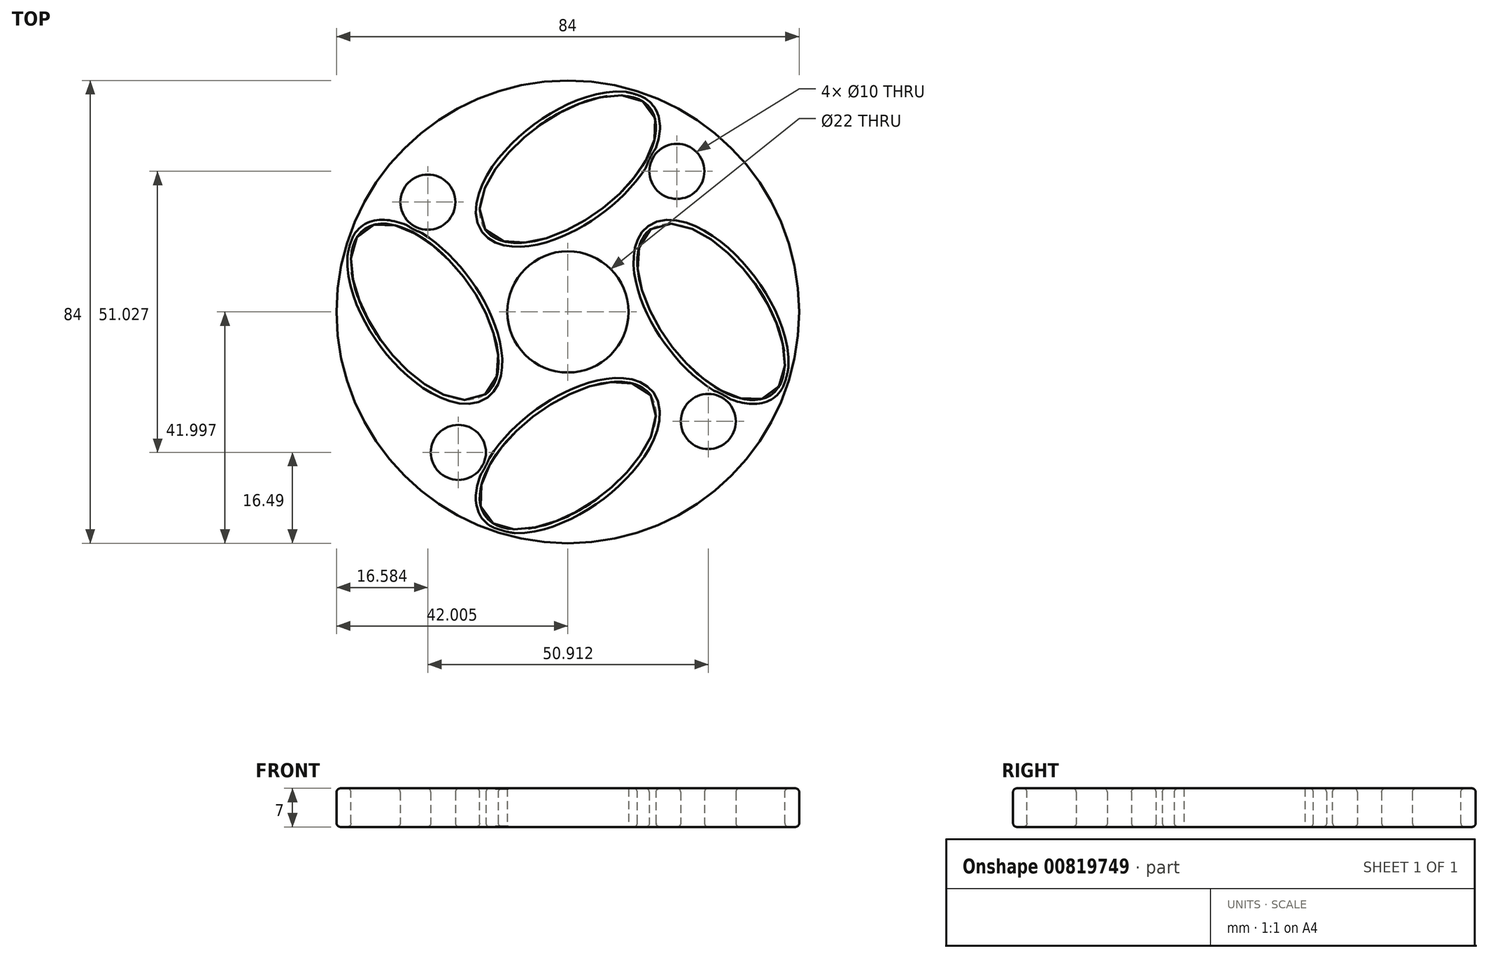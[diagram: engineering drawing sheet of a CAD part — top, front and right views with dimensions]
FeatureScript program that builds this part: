
annotation { "Feature Type Name" : "Feature", "Feature Type Description" : "" }
export const myFeature = defineFeature(function(context is Context, id is Id, definition is map)
    precondition{}
    {
        {
            var Q0;
            Q0=qCreatedBy(makeId("Top.planeOp"),FACE);
            var sketch = newSketch(context, id + "F0", { "sketchPlane" : qUnion([Q0])});
            skCircle(sketch, "E0", {"center": v(-89.33, 23.05) * mm, "radius": 11 * mm});
            skPoint(sketch, "E1", {"position": v(-100.33, 23.05) * mm});
            skPoint(sketch, "E2", {"position": v(-78.33, 23.05) * mm});
            skEllipse(sketch, "E3", {"center": v(-63.33, 23.05) * mm, "majorRadius": 18.6 * mm, "minorRadius": 9.47 * mm, "majorAxis": v(-0.6, 0.8)});
            skEllipse(sketch, "E4", {"center": v(-115.33, 23.05) * mm, "majorRadius": 18.6 * mm, "minorRadius": 9.47 * mm, "majorAxis": v(0.6, -0.8)});
            skPoint(sketch, "E5", {"position": v(-89.33, 33.96) * mm});
            skPoint(sketch, "E6", {"position": v(-89.33, 11.96) * mm});
            skEllipse(sketch, "E7", {"center": v(-89.33, -3.04) * mm, "majorRadius": 18.6 * mm, "minorRadius": 9.47 * mm, "majorAxis": v(0.8, 0.6)});
            skEllipse(sketch, "E8", {"center": v(-89.33, 48.96) * mm, "majorRadius": 18.6 * mm, "minorRadius": 9.47 * mm, "majorAxis": v(-0.8, -0.6)});
            skCircle(sketch, "E9", {"center": v(-89.33, 23.05) * mm, "radius": 42 * mm});
            skPoint(sketch, "E10", {"position": v(-103.17, 47.9) * mm});
            skPoint(sketch, "E11", {"position": v(-64.63, 37.03) * mm});
            skPoint(sketch, "E12", {"position": v(-75.34, -1.73) * mm});
            skPoint(sketch, "E13", {"position": v(-114.1, 9.12) * mm});
            skLineSegment(sketch, "E14", {"start": v(-75.34, -1.73) * mm, "end": v(-52.33, 8.05) * mm});
            skLineSegment(sketch, "E15", {"start": v(-64.63, 37.03) * mm, "end": v(-74.43, 60.1) * mm});
            skLineSegment(sketch, "E16", {"start": v(-103.17, 47.9) * mm, "end": v(-126.33, 38.05) * mm});
            skLineSegment(sketch, "E17", {"start": v(-114.1, 9.12) * mm, "end": v(-104.33, -14.04) * mm});
            skCircle(sketch, "E18", {"center": v(-109.22, -2.46) * mm, "radius": 5 * mm});
            skCircle(sketch, "E19", {"center": v(-63.83, 3.16) * mm, "radius": 5 * mm});
            skCircle(sketch, "E20", {"center": v(-69.53, 48.57) * mm, "radius": 5 * mm});
            skCircle(sketch, "E21", {"center": v(-114.75, 42.97) * mm, "radius": 5 * mm});
            skLineSegment(sketch, "E22", {"start": v(-134.45, 78.47) * mm, "end": v(-134.45, -24.93) * mm, "construction": true});
            skLineSegment(sketch, "E23", {"start": v(-36.96, -24.93) * mm, "end": v(-134.45, -24.93) * mm, "construction": true});
            skLineSegment(sketch, "E24", {"start": v(-85.7, -24.93) * mm, "end": v(-85.7, 23.05) * mm, "construction": true});
            skLineSegment(sketch, "E25", {"start": v(-85.7, 23.05) * mm, "end": v(-36.96, -24.93) * mm, "construction": true});
            skLineSegment(sketch, "E26", {"start": v(-85.7, 23.05) * mm, "end": v(-134.45, 23.05) * mm, "construction": true});
            skSolve(sketch);
        }
        {
            var Q0;
            Q0 = qSketchRegion(id + "F0", true);
            var Q1;
            Q1=makeQuery(id+"F0.imprint","IMPRINT",FACE,{"disambiguationData":[TD([[makeQuery(id+"F0.imprint","IMPRINT",EDGE,{"derivedFrom":sQuery(id+"F0.wireOp",EDGE,"E0")}),-1.0]])]});
            extrude(context, id + "F1", {"entities" : qUnion([Q0, Q1]), "depth" : 7 * mm, "offsetDistance" : 25 * mm});
        }
        {
            var Q0;
            Q0=makeQuery(id+"F1.opExtrude","CAP_EDGE",EDGE,{"disambiguationData":[OSD([sQuery(id+"F0.wireOp",EDGE,"E9")])],"isStart":false});
            var Q1;
            Q1=makeQuery(id+"F1.opExtrude","CAP_EDGE",EDGE,{"disambiguationData":[OSD([sQuery(id+"F0.wireOp",EDGE,"E4")])],"isStart":false});
            var Q2;
            Q2=makeQuery(id+"F1.opExtrude","CAP_EDGE",EDGE,{"disambiguationData":[OSD([sQuery(id+"F0.wireOp",EDGE,"E8")])],"isStart":false});
            var Q3;
            Q3=makeQuery(id+"F1.opExtrude","CAP_EDGE",EDGE,{"disambiguationData":[OSD([sQuery(id+"F0.wireOp",EDGE,"E3")])],"isStart":false});
            var Q4;
            Q4=makeQuery(id+"F1.opExtrude","CAP_EDGE",EDGE,{"disambiguationData":[OSD([sQuery(id+"F0.wireOp",EDGE,"E7")])],"isStart":false});
            var Q5;
            Q5=makeQuery(id+"F1.opExtrude","CAP_EDGE",EDGE,{"disambiguationData":[OSD([sQuery(id+"F0.wireOp",EDGE,"E18")])],"isStart":false});
            var Q6;
            Q6=makeQuery(id+"F1.opExtrude","CAP_EDGE",EDGE,{"disambiguationData":[OSD([sQuery(id+"F0.wireOp",EDGE,"E21")])],"isStart":false});
            var Q7;
            Q7=makeQuery(id+"F1.opExtrude","CAP_EDGE",EDGE,{"disambiguationData":[OSD([sQuery(id+"F0.wireOp",EDGE,"E20")])],"isStart":false});
            var Q8;
            Q8=makeQuery(id+"F1.opExtrude","CAP_EDGE",EDGE,{"disambiguationData":[OSD([sQuery(id+"F0.wireOp",EDGE,"E19")])],"isStart":false});
            var Q9;
            Q9=makeQuery(id+"F1.opExtrude","CAP_EDGE",EDGE,{"disambiguationData":[OSD([sQuery(id+"F0.wireOp",EDGE,"E9")])],"isStart":true});
            var Q10;
            Q10=makeQuery(id+"F1.opExtrude","CAP_EDGE",EDGE,{"disambiguationData":[OSD([sQuery(id+"F0.wireOp",EDGE,"E7")])],"isStart":true});
            var Q11;
            Q11=makeQuery(id+"F1.opExtrude","CAP_EDGE",EDGE,{"disambiguationData":[OSD([sQuery(id+"F0.wireOp",EDGE,"E3")])],"isStart":true});
            var Q12;
            Q12=makeQuery(id+"F1.opExtrude","CAP_EDGE",EDGE,{"disambiguationData":[OSD([sQuery(id+"F0.wireOp",EDGE,"E8")])],"isStart":true});
            var Q13;
            Q13=makeQuery(id+"F1.opExtrude","CAP_EDGE",EDGE,{"disambiguationData":[OSD([sQuery(id+"F0.wireOp",EDGE,"E4")])],"isStart":true});
            var Q14;
            Q14=makeQuery(id+"F1.opExtrude","CAP_EDGE",EDGE,{"disambiguationData":[OSD([sQuery(id+"F0.wireOp",EDGE,"E18")])],"isStart":true});
            var Q15;
            Q15=makeQuery(id+"F1.opExtrude","CAP_EDGE",EDGE,{"disambiguationData":[OSD([sQuery(id+"F0.wireOp",EDGE,"E21")])],"isStart":true});
            var Q16;
            Q16=makeQuery(id+"F1.opExtrude","CAP_EDGE",EDGE,{"disambiguationData":[OSD([sQuery(id+"F0.wireOp",EDGE,"E20")])],"isStart":true});
            var Q17;
            Q17=makeQuery(id+"F1.opExtrude","CAP_EDGE",EDGE,{"disambiguationData":[OSD([sQuery(id+"F0.wireOp",EDGE,"E19")])],"isStart":true});
            fillet(context, id + "F2", {"entities" : qUnion([Q0, Q1, Q2, Q3, Q4, Q5, Q6, Q7, Q8, Q9, Q10, Q11, Q12, Q13, Q14, Q15, Q16, Q17]), "radius" : .7 * mm, "tangentPropagation" : true, "allowEdgeOverflow" : false});
        }
    });
